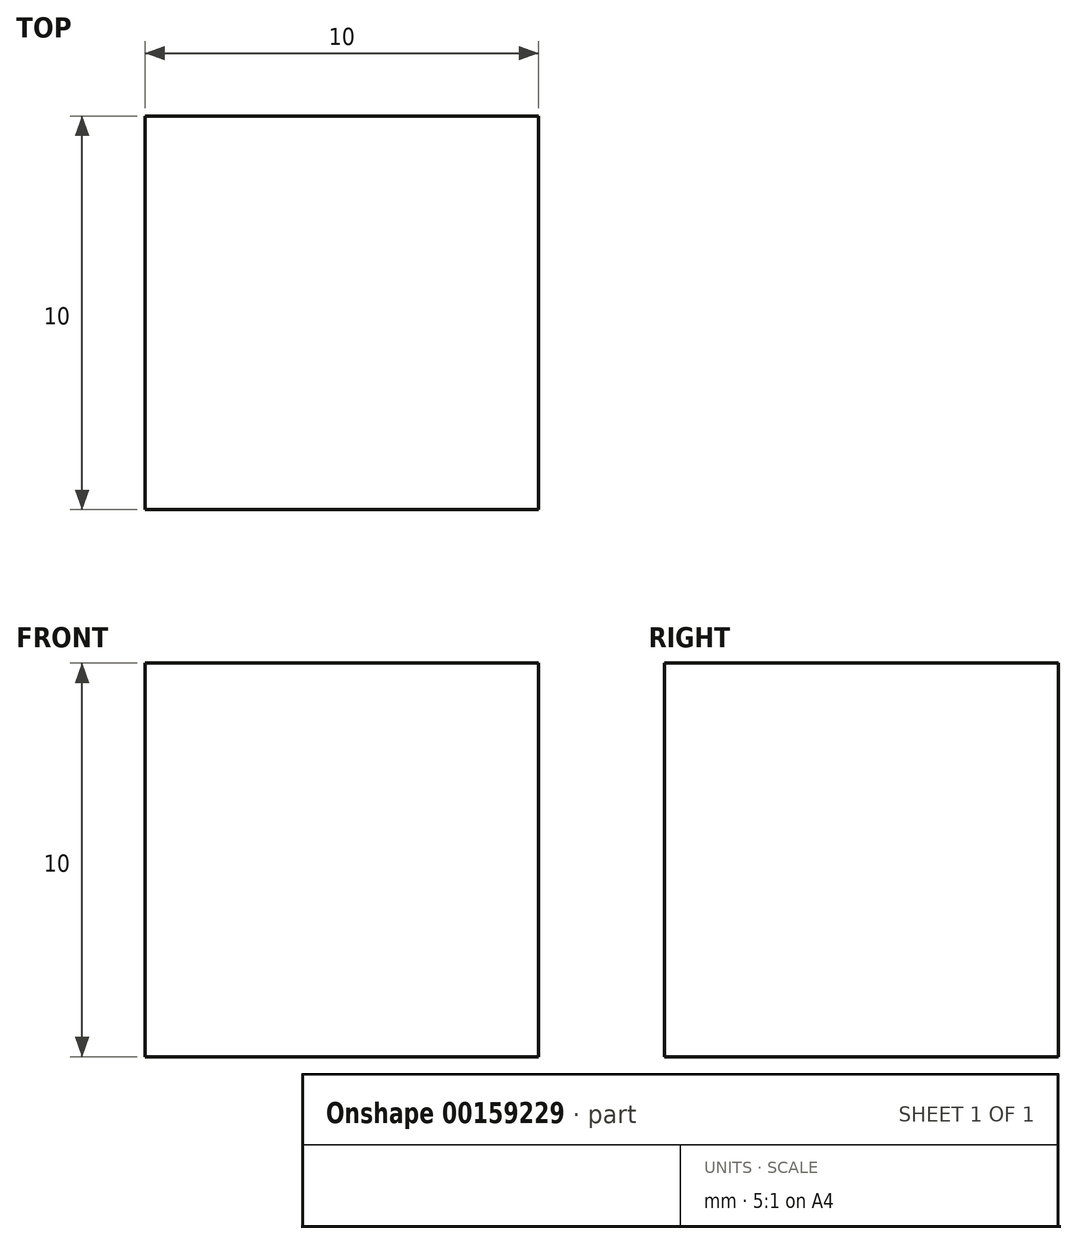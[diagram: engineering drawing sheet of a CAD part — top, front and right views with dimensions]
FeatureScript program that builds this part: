
annotation { "Feature Type Name" : "Feature", "Feature Type Description" : "" }
export const myFeature = defineFeature(function(context is Context, id is Id, definition is map)
    precondition{}
    {
        {
            var Q0;
            Q0=qCreatedBy(makeId("Top.planeOp"),FACE);
            var sketch = newSketch(context, id + "F0", { "sketchPlane" : qUnion([Q0])});
            skLineSegment(sketch, "E0.bottom", {"start": v(-5, 5) * mm, "end": v(5, 5) * mm});
            skLineSegment(sketch, "E0.top", {"start": v(-5, -5) * mm, "end": v(5, -5) * mm});
            skLineSegment(sketch, "E0.left", {"start": v(-5, 5) * mm, "end": v(-5, -5) * mm});
            skLineSegment(sketch, "E0.right", {"start": v(5, 5) * mm, "end": v(5, -5) * mm});
            skPoint(sketch, "E1", {"position": v(0, 0) * mm});
            skPoint(sketch, "E1.positionSnap0", {"position": v(-5, 0) * mm});
            skPoint(sketch, "E1.positionSnap1", {"position": v(0, 5) * mm});
            skSolve(sketch);
        }
        {
            var Q0;
            Q0 = qSketchRegion(id + "F0", true);
            extrude(context, id + "F1", {"entities" : qUnion([Q0]), "depth" : 10 * mm});
        }
    });
